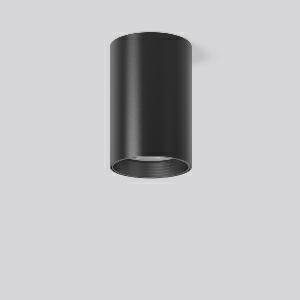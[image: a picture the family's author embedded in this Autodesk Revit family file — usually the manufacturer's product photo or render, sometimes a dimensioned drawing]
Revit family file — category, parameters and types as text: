
# Revit family: heledon_maxi_a_931229_003_1_3319
name_source: partatom
category: Lighting Fixtures
units: mm (PartAtom-declared; Revit-internal decimal feet)

## family parameters
Cut with Voids When Loaded = No
Host = Face
Light Source = No
Part Type = Normal
Room Calculation Point = No
Round Connector Dimension = Use Diameter
Shared = No

## types (1)
- HELEDON maxi A (1 x LED Modul 940, 3800 lm, 4000)
    Apparent Load = 35 VA
    Approval mark = CE
    CIE Flux Codes = 96 100 100 100 100
    Color Rendering = 92
    Color Temperature = 4000
    Default Elevation = 1800 mm
    Description = Series: HELEDON maxi
Cylindrical surface-mounted downlight. Housing: die-cast aluminium, powder-coated. Internal ceiling frame polycarbonate with bayonet mounting. Black plastic ring and recessed LED to prevent glare from the side. Optical assembly with lens made of plastic (polycarbonate) for the best homogeneous light distribution - can be changed without tools. Best colour rendering index Ra>90. Suitable for Ceiling mounting. Easy installation with a separate ceiling frame with bayonet mounting and plug connection. Driver integrated. Connected via plug-in connector. High quality converter without flickering and stroboscopic effect. The following accessories can be mounted without use of tools: interchangeable lenses, decorative glasses, honeycomb louvre, clear and frosted diffusers, white interchangeable plastic ring. 
Colour: deep black, matt (RAL 9005)
Diameter: 123 mm
Height: 183 mm
Lamp: LED
Socket: without socket
Colour temperature: 4000K
Colour rendering index (CRI): 92
System power: 35 W
Rated luminous flux: 3800 lm
Luminous efficiency: 109 lm/W
Control gear: Regulated power supply
Protection class: I
Type of protection: IP 20
    Height = 183 mm
    Lamp = 1 x LED Modul 940
    Lamp Light Flux = 3800 lm
    Lamp count = 1
    Length = 123 mm
    Lifetime = 50000 h
    Luminous efficacy = 109 lm/W
    Manufacturer = RZB
    ModVariant = No
    Model = 931229.003.1
    Mounting Place = Ceiling
    Mounting Type = Surface mounted
    Number of Poles = 1
    OnlyDefault = Yes
    Power Factor = 1
    Product Name = HELEDON maxi A
    Product group = Surface mounted downlights
    ProductGroupID = 302
    Protection Class = Protection class I
    Protection Degree = IP 20
    RLX_Detail_Level = 1
    RLX_Emergency_Light_Flux = 0 lm
    RLX_Emergency_Type = 0
    RLX_Emergency_Type_DB = No
    RlxData = <blob elided: 98605 chars, md5=e782cd1e>
    Socket = socket
    Standby Power = 0 W
    System Light Flux = 3800 lm
    System Power = 35 W
    Type Comments = Product without accessories
    Type Image = 931193.003.jpg
    URL = http://relux.com
    VarID = ---
    Voltage = 230 V
    Voltage Range = 220-240 V
    Weight = 0.00 kg
    Width = 0 mm  [stored 0 ft]

note: [stored X ft] marks values corroborated as IEEE doubles in the binary element streams (Revit-internal decimal feet)

## geometry (parser evidence)
native form markers: Blend x4, Sweep x10
no freeform markers — native parametric forms only
